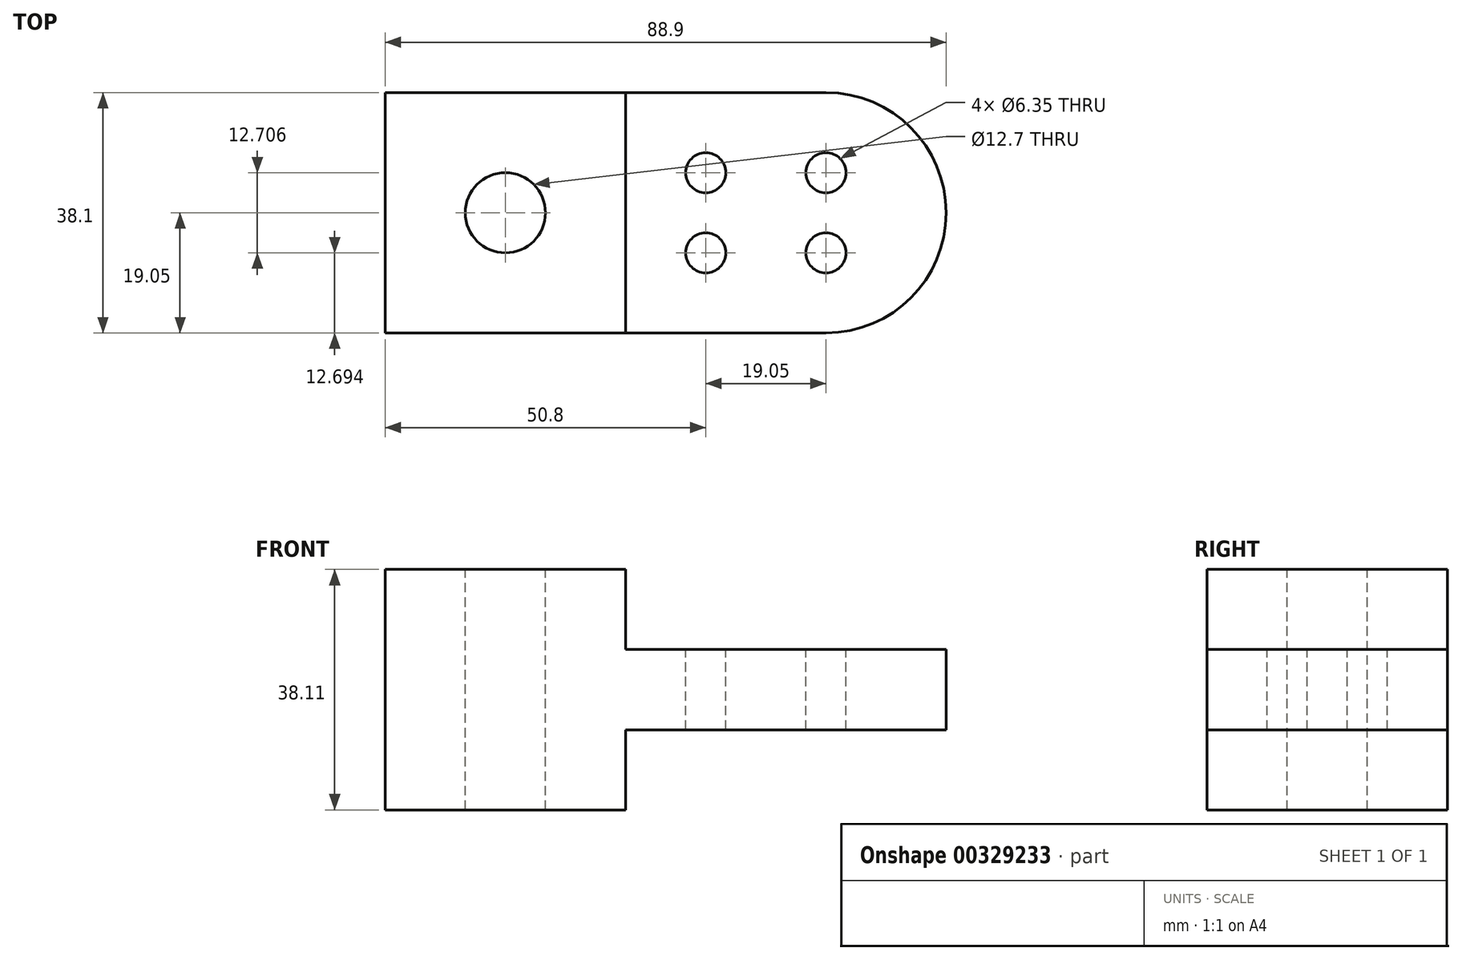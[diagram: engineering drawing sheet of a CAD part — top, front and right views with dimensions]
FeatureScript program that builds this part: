
annotation { "Feature Type Name" : "Feature", "Feature Type Description" : "" }
export const myFeature = defineFeature(function(context is Context, id is Id, definition is map)
    precondition{}
    {
        {
            var Q0;
            Q0=qCreatedBy(makeId("Front.planeOp"),FACE);
            var sketch = newSketch(context, id + "F0", { "sketchPlane" : qUnion([Q0])});
            skLineSegment(sketch, "E0", {"start": v(0, 0) * mm, "end": v(0, 38.1) * mm});
            skLineSegment(sketch, "E1", {"start": v(0, 38.1) * mm, "end": v(38.1, 38.1) * mm});
            skLineSegment(sketch, "E2", {"start": v(38.1, 38.1) * mm, "end": v(38.1, 25.4) * mm});
            skLineSegment(sketch, "E3", {"start": v(38.1, 25.4) * mm, "end": v(88.9, 25.4) * mm});
            skLineSegment(sketch, "E4", {"start": v(88.9, 25.4) * mm, "end": v(88.9, 12.7) * mm});
            skLineSegment(sketch, "E5", {"start": v(88.9, 12.7) * mm, "end": v(38.1, 12.7) * mm});
            skLineSegment(sketch, "E6", {"start": v(38.1, 12.7) * mm, "end": v(38.1, 0) * mm});
            skLineSegment(sketch, "E7", {"start": v(38.1, 0) * mm, "end": v(0, 0) * mm});
            skSolve(sketch);
        }
        {
            var Q0;
            Q0 = qSketchRegion(id + "F0", true);
            extrude(context, id + "F1", {"entities" : qUnion([Q0]), "depth" : 38.1 * mm});
        }
        {
            var Q0;
            Q0=makeQuery(id+"F1.opExtrude","SWEPT_FACE",FACE,{"disambiguationData":[OSD([sQuery(id+"F0.wireOp",EDGE,"E3")])]});
            var sketch = newSketch(context, id + "F2", { "sketchPlane" : qUnion([Q0])});
            skLineSegment(sketch, "E8", {"start": v(38.1, 0) * mm, "end": v(38.1, -38.1) * mm});
            skLineSegment(sketch, "E9", {"start": v(38.1, -38.1) * mm, "end": v(69.85, -38.1) * mm});
            skLineSegment(sketch, "E10", {"start": v(69.85, 0) * mm, "end": v(38.1, 0) * mm});
            skArc(sketch, "E11", {"start": v(69.85, -38.1) * mm, "mid": v(88.9, -19.05) * mm, "end": v(69.85, 0) * mm});
            skSolve(sketch);
        }
        {
            var Q0;
            {var subQ0=sQuery(id+"F2.wireOp",EDGE,"E11");var subQ1=sQuery(id+"F0.wireOp",EDGE,"E3");var subQ2=makeQuery(id+"F1.opExtrude","CAP_EDGE",EDGE,{"disambiguationData":[OSD([subQ1])],"isStart":true});var subQ3=makeQuery(id+"F2.imprint","INTERSECT",VERTEX,{"derivedFrom":[subQ2,sQuery(id+"F2.wireOp",EDGE,"E10"),subQ0]});Q0=makeQuery(id+"F2.imprint","IMPRINT",FACE,{"disambiguationData":[TD([[makeQuery(id+"F2.imprint","IMPRINT",EDGE,{"disambiguationData":[TD([[subQ3,1.0]])],"derivedFrom":subQ0}),-1.0]])]});}
            var Q1;
            {var subQ0=sQuery(id+"F2.wireOp",EDGE,"E11");var subQ1=sQuery(id+"F0.wireOp",EDGE,"E3");var subQ2=makeQuery(id+"F1.opExtrude","CAP_EDGE",EDGE,{"disambiguationData":[OSD([subQ1])],"isStart":false});var subQ3=makeQuery(id+"F2.imprint","INTERSECT",VERTEX,{"derivedFrom":[subQ2,sQuery(id+"F2.wireOp",EDGE,"E9"),subQ0]});Q1=makeQuery(id+"F2.imprint","IMPRINT",FACE,{"disambiguationData":[TD([[makeQuery(id+"F2.imprint","IMPRINT",EDGE,{"disambiguationData":[TD([[subQ3,-1.0]])],"derivedFrom":subQ0}),-1.0]])]});}
            extrude(context, id + "F3", {"entities" : qUnion([Q0, Q1]), "operationType" : NewBodyOperationType.REMOVE, "endBound" : BoundingType.THROUGH_ALL, "oppositeDirection" : true, "depth" : 25.4 * mm});
        }
        {
            var Q0;
            Q0=makeQuery(id+"F1.opExtrude","SWEPT_FACE",FACE,{"disambiguationData":[OSD([sQuery(id+"F0.wireOp",EDGE,"E1")])]});
            var sketch = newSketch(context, id + "F4", { "sketchPlane" : qUnion([Q0])});
            skCircle(sketch, "E12", {"center": v(19.05, -19.05) * mm, "radius": 6.35 * mm});
            skCircle(sketch, "E13", {"center": v(50.8, -12.7) * mm, "radius": 3.18 * mm});
            skCircle(sketch, "E14", {"center": v(50.8, -25.4) * mm, "radius": 3.18 * mm});
            skCircle(sketch, "E15", {"center": v(69.85, -25.4) * mm, "radius": 3.18 * mm});
            skCircle(sketch, "E16", {"center": v(69.85, -12.7) * mm, "radius": 3.18 * mm});
            skSolve(sketch);
        }
        {
            var Q0;
            Q0 = qSketchRegion(id + "F4", true);
            extrude(context, id + "F5", {"entities" : qUnion([Q0]), "operationType" : NewBodyOperationType.REMOVE, "endBound" : BoundingType.THROUGH_ALL, "oppositeDirection" : true, "depth" : 25.4 * mm});
        }
    });
